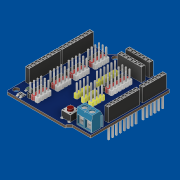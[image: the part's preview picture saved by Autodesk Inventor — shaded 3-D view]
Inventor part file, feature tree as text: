
AUTODESK INVENTOR PART (.ipt)
format: ipt  version: 2019 (Build 230136000, 136)  size: 4,599,296 bytes
history: native  units: in
note: dims shown in document units (in); Inventor stores cm internally (conversion verified against a paired STEP export)
features: projected_geometry x57, extrude x38, sketch x38, chamfer x4, fillet x2
ambient origin geometry x8: Origin, YZ Plane, XZ Plane, XY Plane, X Axis, Y Axis, Z Axis, Center Point
bodies: Solid1 (feature_tree)
feature tree (139):
  extrude  "Extrusion1"  Depth=0.1114in
  extrude  "Extrusion2"  Depth=0.1114in
  extrude  "Extrusion3"  Depth=0.5626in
  extrude  "Extrusion4"  Depth=0.0787in
  chamfer  "Chamfer1"  Distance=0.065in
  extrude  "Extrusion5"  Depth=0.826in
  extrude  "Extrusion6"  Depth=0.826in
  chamfer  "Chamfer2"  Distance=0.3543in
  chamfer  "Chamfer3"  Distance=0.0039in
  extrude  "Extrusion7"  Depth=0.0079in
  extrude  "Extrusion8"  Depth=0.0079in
  extrude  "Extrusion9"  Depth=0.0079in
  extrude  "Extrusion10"  Depth=0.0079in
  extrude  "Extrusion11"  Depth=0.0079in
  extrude  "Extrusion12"  Depth=0.0079in
  extrude  "Extrusion13"  Depth=0.0079in
  extrude  "Extrusion14"  Depth=0.0079in
  extrude  "Extrusion15"  Depth=0.0071in
  extrude  "Extrusion16"  Depth=0.0079in
  extrude  "Extrusion17"  Depth=0.0039in
  extrude  "Extrusion18"  Depth=0.0079in
  extrude  "Extrusion19"  Depth=0.0079in
  extrude  "Extrusion20"  Depth=0.0079in
  chamfer  "Chamfer4"  Distance=0.0079in
  extrude  "Extrusion21"  Depth=0.0079in
  extrude  "Extrusion22"  Depth=0.826in
  extrude  "Extrusion23"  Depth=0.826in
  extrude  "Extrusion24"  Depth=0.0906in
  extrude  "Extrusion25"  Depth=0.0945in
  extrude  "Extrusion26"  Depth=0.0945in
  extrude  "Extrusion27"  Depth=0.0945in
  extrude  "Extrusion28"  Depth=0.0945in
  fillet  "Fillet1"  Radius=0.0945in
  extrude  "Extrusion29"  Depth=0.0945in
  extrude  "Extrusion30"  Depth=0.0945in
  extrude  "Extrusion31"  Depth=0.0945in
  fillet  "Fillet2"  Radius=0.0945in
  extrude  "Extrusion32"  Depth=0.0945in
  extrude  "Extrusion33"  Depth=0.0945in
  extrude  "Extrusion34"  Depth=0.0945in
  extrude  "Extrusion35"  Depth=0.0945in
  extrude  "Extrusion36"  Depth=0.0906in
  extrude  "Extrusion37"  Depth=0.0945in
  extrude  "Extrusion38"  Depth=0.0039in
  sketch  "Sketch1"  dims[d8=0.0965in d10=0.1114in]
  sketch  "Sketch2"  dims[d11=0.1114in d13=0.1114in]
  sketch  "Sketch3"  dims[d14=0.1114in d19=0.5626in]
  sketch  "Sketch4"  dims[d20=0.1087in d21=0.0787in]
  sketch  "Sketch5"  dims[d22=0.0787in]
  sketch  "Sketch6"  dims[d25=0.0394in]
  sketch  "Sketch7"  dims[d26=0.0394in]
  sketch  "Sketch8"  dims[d27=0.1378in]
  sketch  "Sketch9"  dims[d28=0.0984in]
  sketch  "Sketch10"  dims[d29=0.1693in]
  sketch  "Sketch11"  dims[d30=0.0984in]
  sketch  "Sketch12"  dims[d31=0.1772in]
  sketch  "Sketch13"  dims[d32=0.0984in]
  sketch  "Sketch14"  dims[d33=0.1772in d34=0.065in d35=0.0in]
  projected_geometry  "Projected Loop1"
  sketch  "Sketch15"  dims[d36=0.0984in d37=0.826in]
  sketch  "Sketch16"  dims[d38=0.0984in d39=0.826in]
  sketch  "Sketch17"  dims[d40=0.0484in]
  sketch  "Sketch18"  dims[d41=0.0484in]
  sketch  "Sketch19"  dims[d42=0.0354in]
  sketch  "Sketch20"  dims[d43=0.0307in]
  sketch  "Sketch23"  dims[d44=0.0984in]
  sketch  "Sketch25"  dims[d45=0.622in]
  projected_geometry  "Projected Loop2"
  projected_geometry  "Projected Loop3"
  projected_geometry  "Projected Loop4"
  projected_geometry  "Projected Loop5"
  projected_geometry  "Projected Loop6"
  projected_geometry  "Projected Loop7"
  projected_geometry  "Projected Loop8"
  projected_geometry  "Projected Loop9"
  projected_geometry  "Projected Loop10"
  sketch  "Sketch26"  dims[d46=0.0307in]
  projected_geometry  "Projected Loop11"
  projected_geometry  "Projected Loop12"
  projected_geometry  "Projected Loop13"
  projected_geometry  "Projected Loop14"
  projected_geometry  "Projected Loop15"
  projected_geometry  "Projected Loop16"
  projected_geometry  "Projected Loop17"
  projected_geometry  "Projected Loop18"
  projected_geometry  "Projected Loop19"
  projected_geometry  "Projected Loop20"
  projected_geometry  "Projected Loop21"
  projected_geometry  "Projected Loop22"
  projected_geometry  "Projected Loop23"
  projected_geometry  "Projected Loop24"
  projected_geometry  "Projected Loop25"
  projected_geometry  "Projected Loop26"
  projected_geometry  "Projected Loop27"
  projected_geometry  "Projected Loop28"
  projected_geometry  "Projected Loop29"
  projected_geometry  "Projected Loop30"
  projected_geometry  "Projected Loop31"
  projected_geometry  "Projected Loop32"
  projected_geometry  "Projected Loop33"
  projected_geometry  "Projected Loop34"
  projected_geometry  "Projected Loop35"
  projected_geometry  "Projected Loop36"
  projected_geometry  "Projected Loop37"
  projected_geometry  "Projected Loop38"
  projected_geometry  "Projected Loop39"
  projected_geometry  "Projected Loop40"
  sketch  "Sketch27"  dims[d47=0.0484in]
  projected_geometry  "Projected Loop41"
  projected_geometry  "Projected Loop42"
  projected_geometry  "Projected Loop43"
  projected_geometry  "Projected Loop44"
  projected_geometry  "Projected Loop45"
  projected_geometry  "Projected Loop46"
  projected_geometry  "Projected Loop47"
  projected_geometry  "Projected Loop48"
  projected_geometry  "Projected Loop49"
  projected_geometry  "Projected Loop50"
  projected_geometry  "Projected Loop51"
  projected_geometry  "Projected Loop52"
  sketch  "Sketch28"  dims[d48=0.0984in]
  sketch  "Sketch29"  dims[d49=0.826in]
  sketch  "Sketch30"  dims[d50=0.0787in]
  sketch  "Sketch31"  dims[d51=0.0484in]
  sketch  "Sketch32"  dims[d52=0.622in]
  sketch  "Sketch33"  dims[d53=0.0984in]
  sketch  "Sketch34"  dims[d54=0.0177in]
  sketch  "Sketch35"  dims[d55=0.5283in]
  sketch  "Sketch36"  dims[d56=0.622in]
  sketch  "Sketch37"  dims[d57=0.0984in]
  sketch  "Sketch38"  dims[d58=0.1102in d59=0.3543in d60=0.0in]
  sketch  "Sketch39"  dims[d61=0.0906in]
  sketch  "Sketch40"  dims[d62=0.0945in]
  projected_geometry  "Projected Loop53"
  sketch  "Sketch41"  dims[d63=0.0039in d64=0.0039in d66=0.0079in d74=0.0079in d75=0.0079in d76=0.0079in d77=0.0079in d78=0.0079in d79=0.0079in d81=0.0079in d82=0.0071in d83=0.0079in d84=0.0039in d85=0.0079in d86=0.0079in d87=0.0079in d88=0.0079in d89=0.0079in d94=0.826in d95=0.826in d96=0.0906in d97=0.0945in d98=0.0945in d99=0.0945in d100=0.0945in d101=0.0945in d102=0.0945in d105=0.0945in d106=0.0945in d107=0.0945in d108=0.0945in d109=0.0945in d110=0.0945in d111=0.0945in d112=0.0906in d113=0.0945in d114=0.0039in d115=0.0079in d116=0.0945in d117=0.0945in d118=0.0945in d119=0.0945in d120=0.0945in d121=0.0945in d122=0.0945in d123=0.0079in d124=0.0079in d125=0.0079in d126=0.0079in d127=0.0079in d128=0.0079in d129=0.0079in d130=0.0071in d131=0.826in d132=0.0945in d133=0.0079in d134=0.0039in d135=0.0945in d136=0.0945in d137=0.0945in d138=0.0945in d139=0.0945in d140=0.0079in d141=0.0079in d142=0.0079in d143=0.0079in d144=0.0079in d145=0.0079in d146=0.622in d147=0.0945in d148=0.0906in d149=0.0039in d150=0.0079in d151=0.0945in d152=0.0945in d153=0.0945in d154=0.0945in d155=0.0945in d156=0.0079in d157=0.0079in d158=0.0079in d159=0.0079in d160=0.0079in d161=0.0079in d162=0.0945in d163=0.0906in d164=0.0039in d165=0.0079in d166=0.0079in d167=0.0945in d168=0.0945in d169=0.0079in d170=0.0079in d171=0.0071in d172=0.0197in d173=0.0in d174=0.0315in d175=0.0315in d176=0.0315in d177=0.0315in d178=0.0315in d179=0.0315in d180=0.0315in d181=0.0315in d182=0.0315in d183=0.0315in d184=0.0315in d185=0.0315in d186=0.0315in d187=0.0315in d188=0.0315in d189=0.0315in d190=0.0315in d191=0.0315in d192=0.0315in d193=0.0315in d194=0.0315in d195=0.0315in d196=0.0315in d197=0.0315in d198=0.0315in d199=0.0315in d200=0.0315in d201=0.0315in d202=0.0315in d203=0.0315in d204=0.0315in d205=0.0315in d206=0.0315in d207=0.0315in d208=0.0315in d209=0.0315in d210=0.0315in d211=0.0315in d212=0.0315in d213=0.0315in d214=0.0315in d215=0.0315in d216=0.0315in d217=0.0315in d218=0.0315in d219=0.0315in d220=0.0315in d221=0.0315in d222=0.0315in d223=0.0315in d224=0.0315in d225=0.0315in d226=0.0315in d227=0.0315in d228=0.0315in d229=0.0315in d230=0.0315in d231=0.0315in d232=0.2756in d233=0.0in d234=0.0197in d235=0.0787in d236=45.0deg d237=0.3937in d238=0.2992in d239=0.0343in d240=0.0622in d241=0.3937in d242=0.0in d243=0.1354in d244=0.0984in d245=0.0984in d246=0.0157in d247=0.1969in d249=0.1091in d250=0.0283in d251=0.1181in d252=0.0in d253=0.0118in d254=0.1457in d255=45.0deg d256=0.0787in d257=0.1457in d258=45.0deg d259=0.1339in d260=0.1339in d261=0.0157in d262=0.1339in d263=0.0669in d264=0.0157in d265=0.1339in d266=0.0787in d267=0.0in d268=0.0157in d269=0.0in d270=0.0197in d271=0.0197in d272=0.1181in d273=0.0in d274=0.0177in d275=0.0177in d276=0.0177in d277=0.0102in d278=0.2201in d279=0.0346in d280=0.2201in d281=0.0531in d282=0.0in d283=0.1618in d284=0.1126in d285=0.0909in d286=0.0346in d287=0.1575in d288=0.0in d289=0.0787in d290=0.1035in d291=0.0079in d292=0.0in d293=0.2362in d294=0.2362in d295=0.1374in d296=0.5626in d297=0.2209in d298=0.0in d299=0.1358in d300=0.0591in d301=0.0in d302=0.0433in d303=0.0315in d304=0.0315in d305=0.0315in d306=0.0315in d307=0.0315in d308=0.0315in d309=0.0315in d310=0.0315in d311=0.0059in d312=0.0in d313=0.0154in d314=0.0394in d315=0.0323in d316=0.2362in d317=0.0in d318=0.0472in d319=0.0157in d320=0.2756in d321=0.0in d322=0.0114in d323=0.0276in d324=0.0039in d325=0.0114in d326=0.0114in d327=0.0197in d328=0.0in d329=0.0709in d330=0.0004in d331=0.0in d332=0.0114in d333=0.0039in d334=0.0079in d335=0.252in d336=0.0in d337=0.0in d338=0.0197in d339=0.1457in d340=45.0deg d368=0.0945in d369=0.0945in d408=0.1339in d409=0.4087in d476=0.0945in d477=0.0945in d486=0.0945in d487=0.0945in d496=0.0945in d497=0.0945in d506=0.0945in d507=0.0945in d508=0.0945in d509=0.0945in d510=0.0945in d511=0.0945in d512=0.0945in d513=0.0945in d514=0.0945in d515=0.0945in d516=0.0945in d517=0.0945in d518=0.0945in d519=0.0945in d520=0.0945in d521=0.0945in d522=0.0945in d523=0.0945in d524=0.0945in d525=0.0945in d526=0.0945in d527=0.0945in d528=0.0945in d529=0.0945in d530=0.0945in d531=0.0945in d532=0.0945in d533=0.0945in d534=0.0945in d535=0.0945in d536=0.0945in d537=0.0945in d538=0.0945in d539=0.0945in d540=0.0945in d541=0.0945in d542=0.0945in d543=0.0945in d544=0.0945in d545=0.0945in d546=0.0945in d547=0.0945in d548=0.0945in d549=0.0945in d550=0.0945in d551=0.0945in d552=0.0945in d553=0.0945in d554=0.0945in d555=0.0945in d556=0.0945in d557=0.0945in d558=0.0945in d559=0.0945in d560=0.0945in d561=0.0945in d562=0.0945in d563=0.0945in d564=0.0945in d565=0.0945in d566=0.0945in d567=0.0945in d568=0.0945in d569=0.0945in d594=0.6598in d595=0.4087in d596=1.1417in d597=0.4087in d600=0.0945in d601=0.0945in d602=0.0945in d603=0.0945in d604=0.0945in d605=0.0945in d606=0.0945in d607=0.0945in d608=0.0945in d609=0.0945in d610=0.0945in d611=0.0945in d612=0.0945in d613=0.0945in d614=0.0945in d615=0.0945in d616=0.0945in d617=0.0945in d618=0.0945in d619=0.0945in d620=0.0945in d621=0.0945in d622=0.0945in d623=0.0945in d624=1.65in d625=0.4087in d647=0.0945in d648=0.0945in d657=0.0945in d666=0.0945in d667=0.0945in d668=0.0945in d677=0.0945in d678=0.0945in d688=0.7339in d689=0.0197in d690=0.0197in d691=0.0197in d692=0.0197in d693=0.0197in d694=0.0197in d695=0.0197in d696=0.0197in d697=0.0197in d698=0.0197in d699=0.0197in d700=0.0197in d701=0.0197in d702=0.0197in d703=0.0197in d704=0.0197in d705=0.0197in d706=0.0197in d707=0.0197in d708=0.0197in d709=0.0197in d710=0.0197in d711=0.0197in d712=0.0197in d713=0.0197in d714=0.0197in d715=0.0945in d716=0.0945in d717=0.0945in d718=0.0945in d719=0.0945in d720=0.0945in d721=0.0945in d722=0.0945in d723=0.0197in d724=0.0197in d725=0.0197in d726=0.0197in d727=0.0197in d728=0.0197in d729=0.0197in d730=0.0197in d731=0.0197in d732=0.0197in d733=0.0197in d734=0.0197in d735=0.0197in d736=0.0197in d737=0.0197in d738=0.0197in d739=0.0197in d740=0.0197in d741=0.0197in d742=0.0197in d743=0.0197in d744=0.0197in d745=0.0197in d746=0.0197in d747=0.0197in d748=0.0197in d749=0.0945in d750=0.0945in d751=0.0945in d752=0.0945in d753=0.0945in d754=0.0945in d755=0.0945in d756=0.0945in d757=0.0197in d758=0.0197in d759=0.0197in d760=0.0197in d761=0.0197in d762=0.0197in d763=0.0197in d764=0.0197in d765=0.0197in d766=0.0197in d767=0.0197in d768=0.0197in d769=0.0197in d770=0.0197in d771=0.0197in d772=0.0197in d773=0.0197in d774=0.0197in d775=0.0197in d776=0.0197in d777=0.0197in d778=0.0197in d779=0.0197in d780=0.0197in d781=0.0197in d782=0.0197in d783=0.7339in d784=0.7339in d785=0.6142in d786=0.0945in d788=0.0945in d789=0.0945in d790=0.0945in d791=0.0945in d792=0.0945in d793=0.0945in d794=0.0945in d795=0.0945in d796=0.0945in d797=0.0197in d798=0.0197in d799=0.0197in d800=0.0197in d801=0.0197in d802=0.0197in d803=0.0197in d804=0.0197in d805=0.0197in d806=0.0197in d807=0.0197in d808=0.0197in d809=0.0197in d810=0.0197in d811=0.0197in d812=0.0197in d813=0.0197in d814=0.0197in d815=0.0197in d816=0.0197in d817=0.0197in d818=0.0197in d819=0.0197in d820=0.0197in d821=0.0197in d822=0.0197in d823=0.0945in d824=0.0945in d833=0.0197in d834=0.0197in d835=0.0197in d836=0.0197in d837=0.0197in d838=0.0197in d839=0.0197in d840=0.0197in d841=0.0945in d851=0.0945in d852=0.0197in d853=0.0197in d854=0.0197in d855=0.0197in d856=0.0197in d857=0.0197in d858=0.0197in d859=0.0197in d860=0.0945in d861=0.0945in d862=0.0945in d863=0.0945in d864=0.0945in d865=0.0945in d866=0.0945in d867=0.0945in d868=0.0197in d869=0.0197in d870=0.0197in d871=0.0197in d872=0.0197in d873=0.0197in d874=0.0197in d875=0.0197in d876=0.0197in d877=0.0197in d878=0.0197in d879=0.0197in d880=0.0197in d881=0.0197in d882=0.0197in d883=0.0197in d884=0.0197in d885=0.0197in d886=0.0197in d887=0.0197in d888=0.0197in d889=0.0197in d890=0.0197in d891=0.0197in d892=0.0197in d893=0.0197in d894=0.0945in d895=0.0945in d896=0.0197in d897=0.0197in d898=0.0197in d899=0.0197in d900=0.0197in d901=0.0197in d902=0.0197in d903=0.0197in d904=0.0945in d905=0.0945in d906=0.0197in d907=0.0197in d908=0.0197in d909=0.0197in d910=0.0197in d911=0.0197in d912=0.0197in d913=0.0197in d914=0.0945in d915=0.0945in d916=0.0945in d917=0.0945in d918=0.0945in d919=0.0945in d920=0.0945in d921=0.0945in d922=0.0197in d923=0.0197in d924=0.0197in d925=0.0197in d926=0.0197in d927=0.0197in d928=0.0197in d929=0.0197in d930=0.0197in d931=0.0197in d932=0.0197in d933=0.0197in d934=0.0197in d935=0.0197in d936=0.0197in d937=0.0197in d938=0.0197in d939=0.0197in d940=0.0197in d941=0.0197in d942=0.0197in d943=0.0197in d944=0.0197in d945=0.0197in d946=0.0197in d947=0.0197in d948=0.0945in d949=0.0945in d950=0.0197in d951=0.0197in d952=0.0197in d953=0.0197in d954=0.0197in d955=0.0197in d956=0.0197in d957=0.0197in d958=0.0945in d959=0.0945in d960=0.0197in d961=0.0197in d962=0.0197in d963=0.0197in d964=0.0197in d965=0.0197in d966=0.0197in d967=0.0197in d968=0.0945in d969=0.0945in d970=0.0945in d971=0.0945in d972=0.0945in d973=0.0945in d974=0.0945in d975=0.0945in d976=0.0197in d977=0.0197in d978=0.0197in d979=0.0197in d980=0.0197in d981=0.0197in d982=0.0197in d983=0.0197in d984=0.0197in d985=0.0197in d986=0.0197in d987=0.0197in d988=0.0197in d989=0.0197in d990=0.0197in d991=0.0197in d992=0.0197in d993=0.0197in d994=0.0197in d995=0.0197in d996=0.0197in d997=0.0197in d998=0.0197in d999=0.0197in d1000=0.0197in d1001=0.0197in d1002=0.0945in d1003=0.0945in d1004=0.0197in d1005=0.0197in d1006=0.0197in d1007=0.0197in d1008=0.0197in d1009=0.0197in d1010=0.0197in d1011=0.0197in d1012=0.0945in d1013=0.0945in d1014=0.0197in d1015=0.0197in d1016=0.0197in d1017=0.0197in d1018=0.0197in d1019=0.0197in d1020=0.0197in d1021=0.0197in d1022=0.6142in d1023=0.0945in d1024=0.1012in d1025=0.0in d1026=0.0236in d1027=0.0236in d1028=0.0236in d1029=0.0236in d1030=0.0236in d1031=0.0236in d1032=0.0236in d1033=0.0236in d1034=0.0236in d1035=0.0236in d1036=0.0236in d1037=0.0236in d1038=0.0236in d1039=0.0236in d1040=0.0236in d1041=0.0236in d1042=0.0236in d1043=0.0236in d1044=0.0236in d1045=0.0236in d1046=0.0236in d1047=0.0236in d1048=0.0236in d1049=0.0236in d1050=0.0236in d1051=0.0236in d1052=0.0236in d1053=0.0236in d1054=0.0236in d1055=0.0236in d1056=0.0236in d1057=0.0236in d1058=0.0236in d1059=0.0236in d1060=0.0236in d1061=0.0236in d1062=0.0236in d1063=0.0236in d1064=0.0236in d1065=0.0236in d1066=0.0236in d1067=0.0236in d1068=0.0236in d1069=0.0236in d1070=0.0236in d1071=0.0236in d1072=0.0236in d1073=0.0236in d1074=0.0236in d1075=0.0236in d1076=0.0236in d1077=0.0236in d1078=0.0236in d1079=0.0236in d1080=0.0236in d1081=0.0236in d1082=0.0236in d1083=0.0236in d1084=0.0236in d1085=0.0236in d1086=0.0236in d1087=0.0236in d1088=0.0236in d1089=0.0236in d1090=0.0236in d1091=0.0236in d1092=0.0236in d1093=0.0236in d1094=0.0236in d1095=0.0236in d1096=0.0236in d1097=0.0236in d1098=0.0236in d1099=0.0236in d1100=0.0236in d1101=0.0236in d1102=0.0236in d1103=0.0236in d1104=0.0236in d1105=0.0236in d1106=0.0236in d1107=0.0236in d1108=0.0236in d1109=0.0236in d1110=0.0236in d1111=0.0236in d1112=0.0236in d1113=0.0236in d1114=0.0236in d1115=0.0236in d1116=0.0236in d1117=0.0236in d1118=0.0236in d1119=0.0236in d1120=0.0236in d1121=0.0236in d1122=0.0236in d1123=0.0236in d1124=0.0236in d1125=0.0236in d1126=0.0236in d1127=0.0236in d1128=0.0236in d1129=0.0236in d1130=0.0236in d1131=0.0236in d1132=0.0236in d1133=0.0236in d1134=0.0236in d1135=0.0236in d1136=0.0236in d1137=0.0236in d1138=0.0236in d1139=0.0236in d1140=0.0236in d1141=0.0236in d1142=0.0236in d1143=0.0236in d1144=0.0236in d1145=0.0236in d1146=0.0236in d1147=0.0236in d1148=0.0236in d1149=0.0236in d1150=0.0236in d1151=0.0236in d1152=0.0236in d1153=0.0236in d1154=0.0236in d1155=0.0236in d1156=0.0236in d1157=0.0236in d1158=0.0236in d1159=0.0236in d1160=0.0236in d1161=0.0236in d1162=0.0236in d1163=0.0236in d1164=0.0236in d1165=0.0236in d1166=0.0236in d1167=0.0236in d1168=0.0236in d1169=0.0236in d1170=0.0236in d1171=0.0236in d1172=0.0236in d1173=0.0236in d1174=0.0236in d1175=0.0236in d1176=0.0236in d1177=0.0236in d1178=0.0236in d1179=0.0236in d1180=0.0236in d1181=0.0236in d1182=0.0236in d1183=0.0236in d1184=0.0236in d1185=0.0236in d1186=0.0236in d1187=0.0236in d1188=0.0236in d1189=0.0236in d1190=0.0236in d1191=0.0236in d1192=0.0236in d1193=0.0236in d1194=0.2362in d1195=0.0in d1196=0.1929in d1197=0.0in d1198=0.3646in d1199=0.0in d1200=0.0268in d1201=0.0in d1202=0.0476in d1203=0.1028in d1204=0.0476in d1205=0.0516in d1206=0.2252in d1207=0.035in d1208=0.0252in d1209=0.0in d1210=0.0126in d1211=0.0126in d1212=0.0in d1213=0.0in d1214=0.0669in d1215=0.031in d1216=0.0669in d1217=0.031in d1218=0.0in d1219=0.0in d1220=0.0476in d1221=0.0302in d1222=0.0in d1223=0.0in d1224=0.0079in d1225=0.0476in d1226=0.1028in d1227=0.0476in d1228=0.2756in d1229=0.1028in d1230=0.0126in d1231=0.0in d1232=0.0177in d1233=0.0177in d1234=0.0177in d1235=0.0177in d1236=0.0252in d1237=0.0in d1238=0.0307in d1239=0.0004in d1240=0.0in d1241=0.0476in d1242=0.0079in d1243=0.0004in d1244=0.0004in d1245=0.0004in d1246=0.0004in d1249=0.0004in d1250=0.0004in d1251=0.1012in d1252=0.0in d1253=0.0004in d1254=0.0in d1255=0.0004in d1256=0.0in d1257=0.0004in d1258=0.0in d1259=0.0004in d1260=0.0in d1261=0.0315in d1262=0.0315in d1263=0.0315in d1264=0.0315in d1265=0.0268in d1266=0.0in d1267=0.0315in d1268=0.0315in d1269=0.0315in d1270=0.0315in d1271=0.0315in d1272=0.0315in d1273=0.0315in d1274=0.0315in d1275=0.0268in d1276=0.0in]
  projected_geometry  "Projected Loop54"
  projected_geometry  "Projected Loop55"
  projected_geometry  "Projected Loop56"
  projected_geometry  "Projected Loop57"
